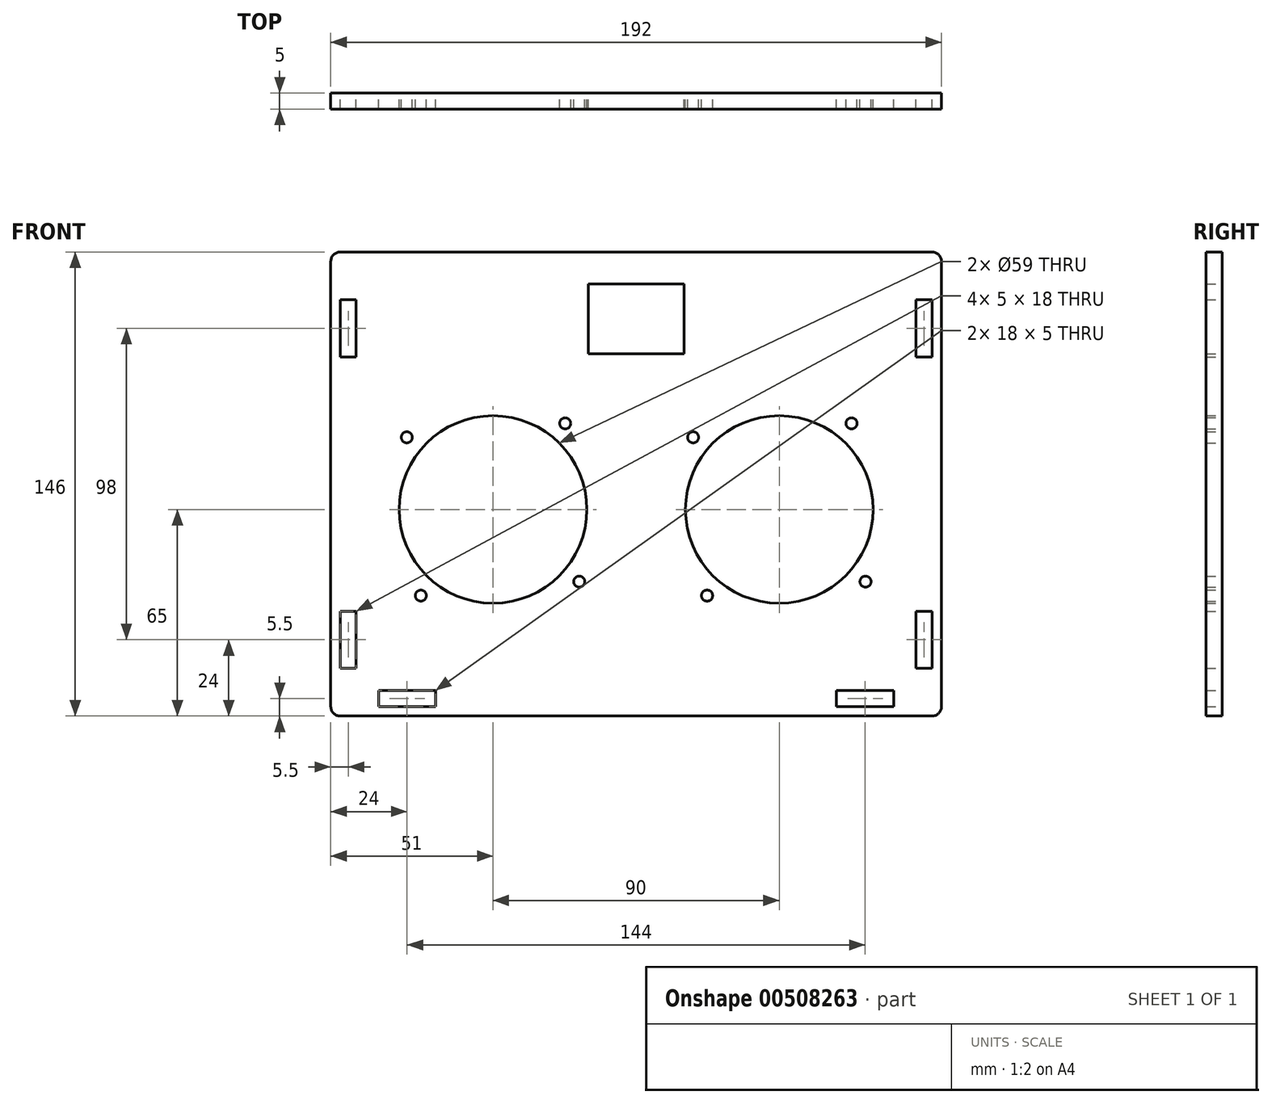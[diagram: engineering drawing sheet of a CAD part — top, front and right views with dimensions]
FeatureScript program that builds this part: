
annotation { "Feature Type Name" : "Feature", "Feature Type Description" : "" }
export const myFeature = defineFeature(function(context is Context, id is Id, definition is map)
    precondition{}
    {
        {
            var Q0;
            Q0=qCreatedBy(makeId("Front.planeOp"),FACE);
            var sketch = newSketch(context, id + "F0", { "sketchPlane" : qUnion([Q0])});
            skLineSegment(sketch, "E0.bottom", {"start": v(-93, 73) * mm, "end": v(93, 73) * mm});
            skLineSegment(sketch, "E0.top", {"start": v(-93, -73) * mm, "end": v(93, -73) * mm});
            skLineSegment(sketch, "E0.left", {"start": v(-96, 70) * mm, "end": v(-96, -70) * mm});
            skLineSegment(sketch, "E0.right", {"start": v(96, 70) * mm, "end": v(96, -70) * mm});
            skPoint(sketch, "E1.visualSharp", {"position": v(-96, 73) * mm});
            skArc(sketch, "E1.filletArc", {"start": v(-93, 73) * mm, "mid": v(-95.12, 72.12) * mm, "end": v(-96, 70) * mm});
            skPoint(sketch, "E2.visualSharp", {"position": v(96, 73) * mm});
            skArc(sketch, "E2.filletArc", {"start": v(96, 70) * mm, "mid": v(95.12, 72.12) * mm, "end": v(93, 73) * mm});
            skPoint(sketch, "E3.visualSharp", {"position": v(96, -73) * mm});
            skArc(sketch, "E3.filletArc", {"start": v(93, -73) * mm, "mid": v(95.12, -72.12) * mm, "end": v(96, -70) * mm});
            skPoint(sketch, "E4.visualSharp", {"position": v(-96, -73) * mm});
            skArc(sketch, "E4.filletArc", {"start": v(-96, -70) * mm, "mid": v(-95.12, -72.12) * mm, "end": v(-93, -73) * mm});
            skLineSegment(sketch, "E5.bottom", {"start": v(-81, 70) * mm, "end": v(-63, 70) * mm});
            skLineSegment(sketch, "E5.top", {"start": v(-81, 65) * mm, "end": v(-63, 65) * mm});
            skLineSegment(sketch, "E5.left", {"start": v(-81, 70) * mm, "end": v(-81, 65) * mm});
            skLineSegment(sketch, "E5.right", {"start": v(-63, 70) * mm, "end": v(-63, 65) * mm});
            skLineSegment(sketch, "E6.bottom", {"start": v(63, 70) * mm, "end": v(81, 70) * mm});
            skLineSegment(sketch, "E6.top", {"start": v(63, 65) * mm, "end": v(81, 65) * mm});
            skLineSegment(sketch, "E6.left", {"start": v(63, 70) * mm, "end": v(63, 65) * mm});
            skLineSegment(sketch, "E6.right", {"start": v(81, 70) * mm, "end": v(81, 65) * mm});
            skLineSegment(sketch, "E7.bottom", {"start": v(93, 58) * mm, "end": v(88, 58) * mm});
            skLineSegment(sketch, "E7.top", {"start": v(93, 40) * mm, "end": v(88, 40) * mm});
            skLineSegment(sketch, "E7.left", {"start": v(93, 58) * mm, "end": v(93, 40) * mm});
            skLineSegment(sketch, "E7.right", {"start": v(88, 58) * mm, "end": v(88, 40) * mm});
            skLineSegment(sketch, "E8.bottom", {"start": v(93, -40) * mm, "end": v(88, -40) * mm});
            skLineSegment(sketch, "E8.top", {"start": v(93, -58) * mm, "end": v(88, -58) * mm});
            skLineSegment(sketch, "E8.left", {"start": v(93, -40) * mm, "end": v(93, -58) * mm});
            skLineSegment(sketch, "E8.right", {"start": v(88, -40) * mm, "end": v(88, -58) * mm});
            skLineSegment(sketch, "E9.bottom", {"start": v(81, -70) * mm, "end": v(63, -70) * mm});
            skLineSegment(sketch, "E9.top", {"start": v(81, -65) * mm, "end": v(63, -65) * mm});
            skLineSegment(sketch, "E9.left", {"start": v(81, -70) * mm, "end": v(81, -65) * mm});
            skLineSegment(sketch, "E9.right", {"start": v(63, -70) * mm, "end": v(63, -65) * mm});
            skLineSegment(sketch, "E10.bottom", {"start": v(-63, -70) * mm, "end": v(-81, -70) * mm});
            skLineSegment(sketch, "E10.top", {"start": v(-63, -65) * mm, "end": v(-81, -65) * mm});
            skLineSegment(sketch, "E10.left", {"start": v(-63, -70) * mm, "end": v(-63, -65) * mm});
            skLineSegment(sketch, "E10.right", {"start": v(-81, -70) * mm, "end": v(-81, -65) * mm});
            skLineSegment(sketch, "E11.bottom", {"start": v(-88, -40) * mm, "end": v(-93, -40) * mm});
            skLineSegment(sketch, "E11.top", {"start": v(-88, -58) * mm, "end": v(-93, -58) * mm});
            skLineSegment(sketch, "E11.left", {"start": v(-88, -58) * mm, "end": v(-88, -40) * mm});
            skLineSegment(sketch, "E11.right", {"start": v(-93, -58) * mm, "end": v(-93, -40) * mm});
            skLineSegment(sketch, "E12.bottom", {"start": v(-88, 40) * mm, "end": v(-93, 40) * mm});
            skLineSegment(sketch, "E12.top", {"start": v(-88, 58) * mm, "end": v(-93, 58) * mm});
            skLineSegment(sketch, "E12.left", {"start": v(-88, 40) * mm, "end": v(-88, 58) * mm});
            skLineSegment(sketch, "E12.right", {"start": v(-93, 40) * mm, "end": v(-93, 58) * mm});
            skCircle(sketch, "E13", {"center": v(45, -8) * mm, "radius": 29.5 * mm});
            skCircle(sketch, "E14", {"center": v(67.7, 19.1) * mm, "radius": 1.75 * mm});
            skCircle(sketch, "E15", {"center": v(17.9, 14.7) * mm, "radius": 1.75 * mm});
            skCircle(sketch, "E16", {"center": v(22.3, -35.1) * mm, "radius": 1.75 * mm});
            skCircle(sketch, "E17", {"center": v(72.1, -30.7) * mm, "radius": 1.75 * mm});
            skLineSegment(sketch, "E18", {"start": v(-96, 0) * mm, "end": v(96, 0) * mm, "construction": true});
            skCircle(sketch, "E19", {"center": v(-45, -8) * mm, "radius": 29.5 * mm});
            skCircle(sketch, "E20", {"center": v(-22.3, 19.1) * mm, "radius": 1.75 * mm});
            skCircle(sketch, "E21", {"center": v(-72.1, 14.7) * mm, "radius": 1.75 * mm});
            skCircle(sketch, "E22", {"center": v(-67.7, -35.1) * mm, "radius": 1.75 * mm});
            skCircle(sketch, "E23", {"center": v(-17.9, -30.7) * mm, "radius": 1.75 * mm});
            skLineSegment(sketch, "E24.bottom", {"start": v(-15, 63) * mm, "end": v(15, 63) * mm});
            skLineSegment(sketch, "E24.top", {"start": v(-15, 41) * mm, "end": v(15, 41) * mm});
            skLineSegment(sketch, "E24.left", {"start": v(-15, 63) * mm, "end": v(-15, 41) * mm});
            skLineSegment(sketch, "E24.right", {"start": v(15, 63) * mm, "end": v(15, 41) * mm});
            skLineSegment(sketch, "E25", {"start": v(0, 0) * mm, "end": v(0, 11.66) * mm, "construction": true});
            skLineSegment(sketch, "E26.bottom", {"start": v(-83, 35) * mm, "end": v(-7, 35) * mm, "construction": true});
            skLineSegment(sketch, "E26.top", {"start": v(-83, -51) * mm, "end": v(-7, -51) * mm, "construction": true});
            skLineSegment(sketch, "E26.left", {"start": v(-83, 35) * mm, "end": v(-83, -51) * mm, "construction": true});
            skLineSegment(sketch, "E26.right", {"start": v(-7, 35) * mm, "end": v(-7, -51) * mm, "construction": true});
            skLineSegment(sketch, "E27.bottom", {"start": v(83, 35) * mm, "end": v(7, 35) * mm, "construction": true});
            skLineSegment(sketch, "E27.top", {"start": v(83, -51) * mm, "end": v(7, -51) * mm, "construction": true});
            skLineSegment(sketch, "E27.left", {"start": v(83, 35) * mm, "end": v(83, -51) * mm, "construction": true});
            skLineSegment(sketch, "E27.right", {"start": v(7, 35) * mm, "end": v(7, -51) * mm, "construction": true});
            skSolve(sketch);
        }
        {
            var Q0;
            Q0=makeQuery(id+"F0.imprint","IMPRINT",FACE,{"disambiguationData":[TD([[makeQuery(id+"F0.imprint","IMPRINT",EDGE,{"derivedFrom":sQuery(id+"F0.wireOp",EDGE,"E0.bottom")}),-1.0]])]});
            var Q1;
            Q1=makeQuery(id+"F0.imprint","IMPRINT",FACE,{"disambiguationData":[TD([[makeQuery(id+"F0.imprint","IMPRINT",EDGE,{"derivedFrom":sQuery(id+"F0.wireOp",EDGE,"E5.bottom")}),-1.0]])]});
            var Q2;
            Q2=makeQuery(id+"F0.imprint","IMPRINT",FACE,{"disambiguationData":[TD([[makeQuery(id+"F0.imprint","IMPRINT",EDGE,{"derivedFrom":sQuery(id+"F0.wireOp",EDGE,"E6.bottom")}),-1.0]])]});
            extrude(context, id + "F1", {"entities" : qUnion([Q0, Q1, Q2]), "depth" : 5 * mm});
        }
    });
